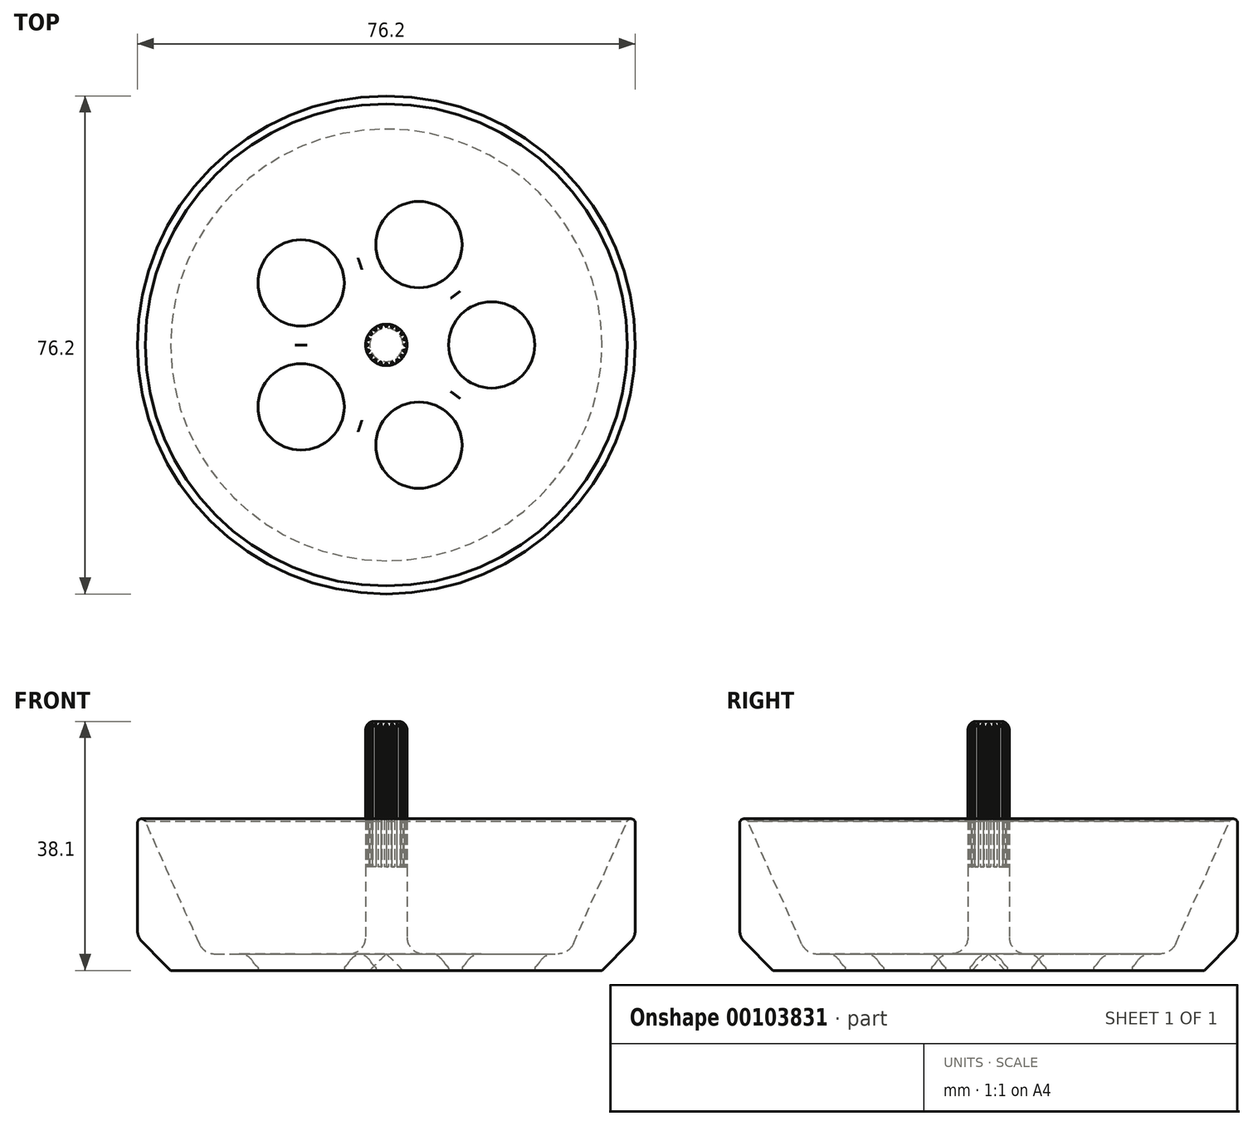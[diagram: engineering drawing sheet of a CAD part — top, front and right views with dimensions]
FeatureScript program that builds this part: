
annotation { "Feature Type Name" : "Feature", "Feature Type Description" : "" }
export const myFeature = defineFeature(function(context is Context, id is Id, definition is map)
    precondition{}
    {
        {
            var Q0;
            Q0=qCreatedBy(makeId("Front.planeOp"),FACE);
            var sketch = newSketch(context, id + "F0", { "sketchPlane" : qUnion([Q0])});
            skLineSegment(sketch, "E0", {"start": v(0, 0) * mm, "end": v(0, 38.1) * mm});
            skLineSegment(sketch, "E1", {"start": v(0, 38.1) * mm, "end": v(1.9, 38.1) * mm});
            skLineSegment(sketch, "E2", {"start": v(38.1, 22.56) * mm, "end": v(38.1, 6.13) * mm});
            skLineSegment(sketch, "E3", {"start": v(2.54, 0) * mm, "end": v(0, 2.54) * mm});
            skPoint(sketch, "E4.visualSharp", {"position": v(3.18, 2.54) * mm});
            skPoint(sketch, "E5.visualSharp", {"position": v(27.94, 2.54) * mm});
            skPoint(sketch, "E6.visualSharp", {"position": v(38.1, 25.4) * mm});
            skArc(sketch, "E6.filletArc", {"start": v(38.1, 22.56) * mm, "mid": v(37.6, 23.18) * mm, "end": v(36.9, 22.83) * mm});
            skPoint(sketch, "E7", {"position": v(16.72, 2.54) * mm});
            skArc(sketch, "E8", {"start": v(8.8, 1.29) * mm, "mid": v(9.08, 0.9) * mm, "end": v(9.43, 0.56) * mm});
            skArc(sketch, "E9", {"start": v(22.83, 0.56) * mm, "mid": v(23.18, 0.9) * mm, "end": v(23.47, 1.29) * mm});
            skLineSegment(sketch, "E10", {"start": v(36.9, 22.83) * mm, "end": v(28.6, 4.05) * mm});
            skLineSegment(sketch, "E11", {"start": v(3.18, 5.08) * mm, "end": v(3.17, 36.83) * mm});
            skLineSegment(sketch, "E12", {"start": v(5.72, 2.54) * mm, "end": v(6.6, 2.54) * mm});
            skLineSegment(sketch, "E13", {"start": v(25.65, 2.54) * mm, "end": v(26.28, 2.54) * mm});
            skPoint(sketch, "E14.visualSharp", {"position": v(23.83, 2.54) * mm});
            skArc(sketch, "E14.filletArc", {"start": v(25.65, 2.54) * mm, "mid": v(24.4, 2.2) * mm, "end": v(23.47, 1.29) * mm});
            skPoint(sketch, "E15.visualSharp", {"position": v(8.43, 2.54) * mm});
            skArc(sketch, "E15.filletArc", {"start": v(8.8, 1.29) * mm, "mid": v(7.86, 2.2) * mm, "end": v(6.6, 2.54) * mm});
            skLineSegment(sketch, "E16", {"start": v(6.6, 2.54) * mm, "end": v(25.65, 2.54) * mm});
            skLineSegment(sketch, "E17", {"start": v(2.54, 0) * mm, "end": v(9.53, 0) * mm});
            skLineSegment(sketch, "E18", {"start": v(22.73, 0) * mm, "end": v(33.02, 0) * mm});
            skLineSegment(sketch, "E19", {"start": v(16.13, 0) * mm, "end": v(16.13, 10.96) * mm});
            skArc(sketch, "E20.filletArc", {"start": v(3.18, 5.08) * mm, "mid": v(3.92, 3.28) * mm, "end": v(5.72, 2.54) * mm});
            skArc(sketch, "E21.filletArc", {"start": v(26.28, 2.54) * mm, "mid": v(27.67, 2.95) * mm, "end": v(28.6, 4.05) * mm});
            skPoint(sketch, "E22.visualSharp", {"position": v(3.17, 38.1) * mm});
            skArc(sketch, "E22.filletArc", {"start": v(3.17, 36.83) * mm, "mid": v(2.8, 37.73) * mm, "end": v(1.9, 38.1) * mm});
            skLineSegment(sketch, "E23", {"start": v(22.73, 0) * mm, "end": v(22.73, 0.36) * mm});
            skLineSegment(sketch, "E24.MirrorCS", {"start": v(9.53, 0) * mm, "end": v(9.53, 0.36) * mm});
            skPoint(sketch, "E25.orphan", {"position": v(11.05, 0) * mm});
            skPoint(sketch, "E26.end.orphan", {"position": v(21.2, 0) * mm});
            skLineSegment(sketch, "E27", {"start": v(9.53, 0) * mm, "end": v(22.73, 0) * mm});
            skPoint(sketch, "E28.newPointB", {"position": v(9.53, 6.48) * mm});
            skArc(sketch, "E28.filletArc", {"start": v(9.52, 0.36) * mm, "mid": v(9.5, 0.47) * mm, "end": v(9.43, 0.56) * mm});
            skPoint(sketch, "E29.newPointB", {"position": v(22.73, 6.48) * mm});
            skArc(sketch, "E29.filletArc", {"start": v(22.83, 0.56) * mm, "mid": v(22.76, 0.47) * mm, "end": v(22.73, 0.36) * mm});
            skLineSegment(sketch, "E30", {"start": v(33.02, 0) * mm, "end": v(37.36, 4.34) * mm});
            skPoint(sketch, "E31.orphan", {"position": v(38.1, 0) * mm});
            skPoint(sketch, "E32.visualSharp", {"position": v(38.1, 5.08) * mm});
            skArc(sketch, "E32.filletArc", {"start": v(37.36, 4.34) * mm, "mid": v(37.9, 5.16) * mm, "end": v(38.1, 6.13) * mm});
            skSolve(sketch);
        }
        {
            var Q0;
            {var subQ1=sQuery(id+"F0.wireOp",EDGE,"E1");Q0=makeQuery(id+"F0.imprint","IMPRINT",FACE,{"disambiguationData":[TD([[makeQuery(id+"F0.imprint","IMPRINT",EDGE,{"derivedFrom":subQ1}),-1.0]])]});}
            var Q1;
            {var subQ1=sQuery(id+"F0.wireOp",EDGE,"E8");Q1=makeQuery(id+"F0.imprint","IMPRINT",FACE,{"disambiguationData":[TD([[makeQuery(id+"F0.imprint","IMPRINT",EDGE,{"derivedFrom":subQ1}),1.0]])]});}
            var Q2;
            {var subQ1=sQuery(id+"F0.wireOp",EDGE,"E9");Q2=makeQuery(id+"F0.imprint","IMPRINT",FACE,{"disambiguationData":[TD([[makeQuery(id+"F0.imprint","IMPRINT",EDGE,{"derivedFrom":subQ1}),1.0]])]});}
            var Q3;
            Q3=makeQuery(id+"F0.imprint","IMPRINT",FACE,{"disambiguationData":[TD([[makeQuery(id+"F0.imprint","IMPRINT",EDGE,{"derivedFrom":sQuery(id+"F0.wireOp",EDGE,"E2")}),-1.0]])]});
            var Q4;
            Q4=sQuery(id+"F0.wireOp",EDGE,"E0");
            revolve(context, id + "F1", {"entities" : qUnion([Q0, Q1, Q2, Q3]), "axis" : qUnion([Q4]), "revolveType" : RevolveType.FULL});
        }
        {
            var Q0;
            {var subQ1=sQuery(id+"F0.wireOp",EDGE,"E8");Q0=makeQuery(id+"F0.imprint","IMPRINT",FACE,{"disambiguationData":[TD([[makeQuery(id+"F0.imprint","IMPRINT",EDGE,{"derivedFrom":subQ1}),1.0]])]});}
            var Q1;
            Q1=sQuery(id+"F0.wireOp",EDGE,"E19");
            revolve(context, id + "F2", {"entities" : qUnion([Q0]), "axis" : qUnion([Q1]), "revolveType" : RevolveType.FULL});
        }
        {
            var Q0;
            Q0=makeQuery(id+"F2.opRevolve","SWEPT_BODY",BODY,{"disambiguationData":[OSD([sQuery(id+"F0.wireOp",EDGE,"E8"),sQuery(id+"F0.wireOp",EDGE,"E15.filletArc"),sQuery(id+"F0.wireOp",EDGE,"E16"),sQuery(id+"F0.wireOp",EDGE,"E26"),sQuery(id+"F0.wireOp",EDGE,"E19")])]});
            var Q1;
            Q1=sQuery(id+"F0.wireOp",EDGE,"E0");
            circularPattern(context, id + "F3", {"entities" : qUnion([Q0]), "axis" : qUnion([Q1]), "angle" : 360 * degree, "instanceCount" : 5, "equalSpace" : true});
        }
        {
            var Q0;
            Q0=makeQuery(id+"F2.opRevolve","SWEPT_BODY",BODY,{"disambiguationData":[OSD([sQuery(id+"F0.wireOp",EDGE,"E8"),sQuery(id+"F0.wireOp",EDGE,"E15.filletArc"),sQuery(id+"F0.wireOp",EDGE,"E16"),sQuery(id+"F0.wireOp",EDGE,"E26"),sQuery(id+"F0.wireOp",EDGE,"E19")])]});
            var Q1;
            Q1=makeQuery(id+"F3.opPattern","COPY",BODY,{"derivedFrom":makeQuery(id+"F2.opRevolve","SWEPT_BODY",BODY,{"disambiguationData":[OSD([sQuery(id+"F0.wireOp",EDGE,"E8"),sQuery(id+"F0.wireOp",EDGE,"E15.filletArc"),sQuery(id+"F0.wireOp",EDGE,"E16"),sQuery(id+"F0.wireOp",EDGE,"E26"),sQuery(id+"F0.wireOp",EDGE,"E19")])]}),"instanceName":"1"});
            var Q2;
            Q2=makeQuery(id+"F3.opPattern","COPY",BODY,{"derivedFrom":makeQuery(id+"F2.opRevolve","SWEPT_BODY",BODY,{"disambiguationData":[OSD([sQuery(id+"F0.wireOp",EDGE,"E8"),sQuery(id+"F0.wireOp",EDGE,"E15.filletArc"),sQuery(id+"F0.wireOp",EDGE,"E16"),sQuery(id+"F0.wireOp",EDGE,"E26"),sQuery(id+"F0.wireOp",EDGE,"E19")])]}),"instanceName":"2"});
            var Q3;
            Q3=makeQuery(id+"F3.opPattern","COPY",BODY,{"derivedFrom":makeQuery(id+"F2.opRevolve","SWEPT_BODY",BODY,{"disambiguationData":[OSD([sQuery(id+"F0.wireOp",EDGE,"E8"),sQuery(id+"F0.wireOp",EDGE,"E15.filletArc"),sQuery(id+"F0.wireOp",EDGE,"E16"),sQuery(id+"F0.wireOp",EDGE,"E26"),sQuery(id+"F0.wireOp",EDGE,"E19")])]}),"instanceName":"3"});
            var Q4;
            Q4=makeQuery(id+"F3.opPattern","COPY",BODY,{"derivedFrom":makeQuery(id+"F2.opRevolve","SWEPT_BODY",BODY,{"disambiguationData":[OSD([sQuery(id+"F0.wireOp",EDGE,"E8"),sQuery(id+"F0.wireOp",EDGE,"E15.filletArc"),sQuery(id+"F0.wireOp",EDGE,"E16"),sQuery(id+"F0.wireOp",EDGE,"E26"),sQuery(id+"F0.wireOp",EDGE,"E19")])]}),"instanceName":"4"});
            var Q5;
            Q5=makeQuery(id+"F1.opRevolve","SWEPT_BODY",BODY,{"disambiguationData":[OSD([sQuery(id+"F0.wireOp",EDGE,"E0"),sQuery(id+"F0.wireOp",EDGE,"E1"),sQuery(id+"F0.wireOp",EDGE,"E2"),sQuery(id+"F0.wireOp",EDGE,"E3"),sQuery(id+"F0.wireOp",EDGE,"E6.filletArc"),sQuery(id+"F0.wireOp",EDGE,"E10"),sQuery(id+"F0.wireOp",EDGE,"E11"),sQuery(id+"F0.wireOp",EDGE,"E12"),sQuery(id+"F0.wireOp",EDGE,"E13"),sQuery(id+"F0.wireOp",EDGE,"E16"),sQuery(id+"F0.wireOp",EDGE,"E17"),sQuery(id+"F0.wireOp",EDGE,"E26"),sQuery(id+"F0.wireOp",EDGE,"E18"),sQuery(id+"F0.wireOp",EDGE,"E20.filletArc"),sQuery(id+"F0.wireOp",EDGE,"E21.filletArc")])]});
            booleanBodies(context, id + "F4", {"operationType" : BooleanOperationType.SUBTRACTION, "tools" : qUnion([Q0, Q1, Q2, Q3, Q4]), "targets" : qUnion([Q5])});
        }
        {
            var Q0;
            Q0=qCreatedBy(makeId("Top.planeOp"),FACE);
            var sketch = newSketch(context, id + "F5", { "sketchPlane" : qUnion([Q0])});
            skCircle(sketch, "E33", {"center": v(0, 0) * mm, "radius": 3.18 * mm});
            skLineSegment(sketch, "E34", {"start": v(0, 2.66) * mm, "end": v(0.3, 3.16) * mm});
            skLineSegment(sketch, "E35.MirrorCS", {"start": v(0, 2.66) * mm, "end": v(-0.3, 3.16) * mm});
            skLineSegment(sketch, "E36.1.0", {"start": v(-0.82, 2.53) * mm, "end": v(-0.68, 3.1) * mm});
            skLineSegment(sketch, "E36.1.1", {"start": v(-0.82, 2.53) * mm, "end": v(-1.27, 2.9) * mm});
            skLineSegment(sketch, "E36.2.0", {"start": v(-1.57, 2.16) * mm, "end": v(-1.6, 2.74) * mm});
            skLineSegment(sketch, "E36.2.1", {"start": v(-1.57, 2.16) * mm, "end": v(-2.1, 2.37) * mm});
            skLineSegment(sketch, "E36.3.0", {"start": v(-2.16, 1.57) * mm, "end": v(-2.37, 2.1) * mm});
            skLineSegment(sketch, "E36.3.1", {"start": v(-2.16, 1.57) * mm, "end": v(-2.74, 1.6) * mm});
            skLineSegment(sketch, "E36.4.0", {"start": v(-2.53, 0.82) * mm, "end": v(-2.9, 1.27) * mm});
            skLineSegment(sketch, "E36.4.1", {"start": v(-2.53, 0.82) * mm, "end": v(-3.1, 0.68) * mm});
            skLineSegment(sketch, "E36.5.0", {"start": v(-2.66, 0) * mm, "end": v(-3.16, 0.3) * mm});
            skLineSegment(sketch, "E36.5.1", {"start": v(-2.66, 0) * mm, "end": v(-3.16, -0.3) * mm});
            skLineSegment(sketch, "E36.6.0", {"start": v(-2.53, -0.82) * mm, "end": v(-3.1, -0.68) * mm});
            skLineSegment(sketch, "E36.6.1", {"start": v(-2.53, -0.82) * mm, "end": v(-2.9, -1.27) * mm});
            skLineSegment(sketch, "E36.7.0", {"start": v(-2.16, -1.57) * mm, "end": v(-2.74, -1.6) * mm});
            skLineSegment(sketch, "E36.7.1", {"start": v(-2.16, -1.57) * mm, "end": v(-2.37, -2.1) * mm});
            skLineSegment(sketch, "E36.8.0", {"start": v(-1.57, -2.16) * mm, "end": v(-2.1, -2.37) * mm});
            skLineSegment(sketch, "E36.8.1", {"start": v(-1.57, -2.16) * mm, "end": v(-1.6, -2.74) * mm});
            skLineSegment(sketch, "E36.9.0", {"start": v(-0.82, -2.53) * mm, "end": v(-1.27, -2.9) * mm});
            skLineSegment(sketch, "E36.9.1", {"start": v(-0.82, -2.53) * mm, "end": v(-0.68, -3.1) * mm});
            skLineSegment(sketch, "E36.10.0", {"start": v(0, -2.66) * mm, "end": v(-0.3, -3.16) * mm});
            skLineSegment(sketch, "E36.10.1", {"start": v(0, -2.66) * mm, "end": v(0.3, -3.16) * mm});
            skLineSegment(sketch, "E36.11.0", {"start": v(0.82, -2.53) * mm, "end": v(0.68, -3.1) * mm});
            skLineSegment(sketch, "E36.11.1", {"start": v(0.82, -2.53) * mm, "end": v(1.27, -2.9) * mm});
            skLineSegment(sketch, "E36.12.0", {"start": v(1.57, -2.16) * mm, "end": v(1.6, -2.74) * mm});
            skLineSegment(sketch, "E36.12.1", {"start": v(1.57, -2.16) * mm, "end": v(2.1, -2.37) * mm});
            skLineSegment(sketch, "E36.13.0", {"start": v(2.16, -1.57) * mm, "end": v(2.37, -2.1) * mm});
            skLineSegment(sketch, "E36.13.1", {"start": v(2.16, -1.57) * mm, "end": v(2.74, -1.6) * mm});
            skLineSegment(sketch, "E36.14.0", {"start": v(2.53, -0.82) * mm, "end": v(2.9, -1.27) * mm});
            skLineSegment(sketch, "E36.14.1", {"start": v(2.53, -0.82) * mm, "end": v(3.1, -0.68) * mm});
            skLineSegment(sketch, "E36.15.0", {"start": v(2.66, 0) * mm, "end": v(3.16, -0.3) * mm});
            skLineSegment(sketch, "E36.15.1", {"start": v(2.66, 0) * mm, "end": v(3.16, 0.3) * mm});
            skLineSegment(sketch, "E36.16.0", {"start": v(2.53, 0.82) * mm, "end": v(3.1, 0.68) * mm});
            skLineSegment(sketch, "E36.16.1", {"start": v(2.53, 0.82) * mm, "end": v(2.9, 1.27) * mm});
            skLineSegment(sketch, "E36.17.0", {"start": v(2.16, 1.57) * mm, "end": v(2.74, 1.6) * mm});
            skLineSegment(sketch, "E36.17.1", {"start": v(2.16, 1.57) * mm, "end": v(2.37, 2.1) * mm});
            skLineSegment(sketch, "E36.18.0", {"start": v(1.57, 2.16) * mm, "end": v(2.1, 2.37) * mm});
            skLineSegment(sketch, "E36.18.1", {"start": v(1.57, 2.16) * mm, "end": v(1.6, 2.74) * mm});
            skLineSegment(sketch, "E36.19.0", {"start": v(0.82, 2.53) * mm, "end": v(1.27, 2.9) * mm});
            skLineSegment(sketch, "E36.19.1", {"start": v(0.82, 2.53) * mm, "end": v(0.68, 3.1) * mm});
            skSolve(sketch);
        }
        {
            var Q0;
            {var subQ0=sQuery(id+"F5.wireOp",EDGE,"E36.3.0");Q0=makeQuery(id+"F5.imprint","IMPRINT",FACE,{"disambiguationData":[TD([[makeQuery(id+"F5.imprint","IMPRINT",EDGE,{"derivedFrom":subQ0}),1.0]])]});}
            var Q1;
            {var subQ0=sQuery(id+"F5.wireOp",EDGE,"E36.4.0");Q1=makeQuery(id+"F5.imprint","IMPRINT",FACE,{"disambiguationData":[TD([[makeQuery(id+"F5.imprint","IMPRINT",EDGE,{"derivedFrom":subQ0}),1.0]])]});}
            var Q2;
            {var subQ0=sQuery(id+"F5.wireOp",EDGE,"E36.5.0");Q2=makeQuery(id+"F5.imprint","IMPRINT",FACE,{"disambiguationData":[TD([[makeQuery(id+"F5.imprint","IMPRINT",EDGE,{"derivedFrom":subQ0}),1.0]])]});}
            var Q3;
            {var subQ0=sQuery(id+"F5.wireOp",EDGE,"E36.6.0");Q3=makeQuery(id+"F5.imprint","IMPRINT",FACE,{"disambiguationData":[TD([[makeQuery(id+"F5.imprint","IMPRINT",EDGE,{"derivedFrom":subQ0}),1.0]])]});}
            var Q4;
            {var subQ0=sQuery(id+"F5.wireOp",EDGE,"E36.7.0");Q4=makeQuery(id+"F5.imprint","IMPRINT",FACE,{"disambiguationData":[TD([[makeQuery(id+"F5.imprint","IMPRINT",EDGE,{"derivedFrom":subQ0}),1.0]])]});}
            var Q5;
            {var subQ0=sQuery(id+"F5.wireOp",EDGE,"E36.8.0");Q5=makeQuery(id+"F5.imprint","IMPRINT",FACE,{"disambiguationData":[TD([[makeQuery(id+"F5.imprint","IMPRINT",EDGE,{"derivedFrom":subQ0}),1.0]])]});}
            var Q6;
            {var subQ0=sQuery(id+"F5.wireOp",EDGE,"E36.9.0");Q6=makeQuery(id+"F5.imprint","IMPRINT",FACE,{"disambiguationData":[TD([[makeQuery(id+"F5.imprint","IMPRINT",EDGE,{"derivedFrom":subQ0}),1.0]])]});}
            var Q7;
            {var subQ0=sQuery(id+"F5.wireOp",EDGE,"E36.10.0");Q7=makeQuery(id+"F5.imprint","IMPRINT",FACE,{"disambiguationData":[TD([[makeQuery(id+"F5.imprint","IMPRINT",EDGE,{"derivedFrom":subQ0}),1.0]])]});}
            var Q8;
            {var subQ0=sQuery(id+"F5.wireOp",EDGE,"E36.11.0");Q8=makeQuery(id+"F5.imprint","IMPRINT",FACE,{"disambiguationData":[TD([[makeQuery(id+"F5.imprint","IMPRINT",EDGE,{"derivedFrom":subQ0}),1.0]])]});}
            var Q9;
            {var subQ0=sQuery(id+"F5.wireOp",EDGE,"E36.12.0");Q9=makeQuery(id+"F5.imprint","IMPRINT",FACE,{"disambiguationData":[TD([[makeQuery(id+"F5.imprint","IMPRINT",EDGE,{"derivedFrom":subQ0}),1.0]])]});}
            var Q10;
            {var subQ0=sQuery(id+"F5.wireOp",EDGE,"E36.13.0");Q10=makeQuery(id+"F5.imprint","IMPRINT",FACE,{"disambiguationData":[TD([[makeQuery(id+"F5.imprint","IMPRINT",EDGE,{"derivedFrom":subQ0}),1.0]])]});}
            var Q11;
            {var subQ0=sQuery(id+"F5.wireOp",EDGE,"E36.14.0");Q11=makeQuery(id+"F5.imprint","IMPRINT",FACE,{"disambiguationData":[TD([[makeQuery(id+"F5.imprint","IMPRINT",EDGE,{"derivedFrom":subQ0}),1.0]])]});}
            var Q12;
            {var subQ0=sQuery(id+"F5.wireOp",EDGE,"E36.15.0");Q12=makeQuery(id+"F5.imprint","IMPRINT",FACE,{"disambiguationData":[TD([[makeQuery(id+"F5.imprint","IMPRINT",EDGE,{"derivedFrom":subQ0}),1.0]])]});}
            var Q13;
            {var subQ0=sQuery(id+"F5.wireOp",EDGE,"E36.16.0");Q13=makeQuery(id+"F5.imprint","IMPRINT",FACE,{"disambiguationData":[TD([[makeQuery(id+"F5.imprint","IMPRINT",EDGE,{"derivedFrom":subQ0}),1.0]])]});}
            var Q14;
            {var subQ0=sQuery(id+"F5.wireOp",EDGE,"E36.17.0");Q14=makeQuery(id+"F5.imprint","IMPRINT",FACE,{"disambiguationData":[TD([[makeQuery(id+"F5.imprint","IMPRINT",EDGE,{"derivedFrom":subQ0}),1.0]])]});}
            var Q15;
            {var subQ0=sQuery(id+"F5.wireOp",EDGE,"E36.18.0");Q15=makeQuery(id+"F5.imprint","IMPRINT",FACE,{"disambiguationData":[TD([[makeQuery(id+"F5.imprint","IMPRINT",EDGE,{"derivedFrom":subQ0}),1.0]])]});}
            var Q16;
            {var subQ0=sQuery(id+"F5.wireOp",EDGE,"E36.19.0");Q16=makeQuery(id+"F5.imprint","IMPRINT",FACE,{"disambiguationData":[TD([[makeQuery(id+"F5.imprint","IMPRINT",EDGE,{"derivedFrom":subQ0}),1.0]])]});}
            var Q17;
            {var subQ0=sQuery(id+"F5.wireOp",EDGE,"E34");Q17=makeQuery(id+"F5.imprint","IMPRINT",FACE,{"disambiguationData":[TD([[makeQuery(id+"F5.imprint","IMPRINT",EDGE,{"derivedFrom":subQ0}),1.0]])]});}
            var Q18;
            {var subQ0=sQuery(id+"F5.wireOp",EDGE,"E36.1.0");Q18=makeQuery(id+"F5.imprint","IMPRINT",FACE,{"disambiguationData":[TD([[makeQuery(id+"F5.imprint","IMPRINT",EDGE,{"derivedFrom":subQ0}),1.0]])]});}
            var Q19;
            {var subQ0=sQuery(id+"F5.wireOp",EDGE,"E36.2.0");Q19=makeQuery(id+"F5.imprint","IMPRINT",FACE,{"disambiguationData":[TD([[makeQuery(id+"F5.imprint","IMPRINT",EDGE,{"derivedFrom":subQ0}),1.0]])]});}
            extrude(context, id + "F6", {"entities" : qUnion([Q0, Q1, Q2, Q3, Q4, Q5, Q6, Q7, Q8, Q9, Q10, Q11, Q12, Q13, Q14, Q15, Q16, Q17, Q18, Q19]), "depth" : 42.16 * mm, "hasSecondDirection" : true, "secondDirectionOppositeDirection" : false, "secondDirectionDepth" : 15.88 * mm});
        }
        {
            var Q0;
            Q0=makeQuery(id+"F6.opExtrude","SWEPT_BODY",BODY,{"disambiguationData":[OSD([sQuery(id+"F5.wireOp",EDGE,"E33"),sQuery(id+"F5.wireOp",EDGE,"E36.16.0"),sQuery(id+"F5.wireOp",EDGE,"E36.16.1")])]});
            var Q1;
            Q1=makeQuery(id+"F6.opExtrude","SWEPT_BODY",BODY,{"disambiguationData":[OSD([sQuery(id+"F5.wireOp",EDGE,"E33"),sQuery(id+"F5.wireOp",EDGE,"E36.17.0"),sQuery(id+"F5.wireOp",EDGE,"E36.17.1")])]});
            var Q2;
            Q2=makeQuery(id+"F6.opExtrude","SWEPT_BODY",BODY,{"disambiguationData":[OSD([sQuery(id+"F5.wireOp",EDGE,"E33"),sQuery(id+"F5.wireOp",EDGE,"E36.18.0"),sQuery(id+"F5.wireOp",EDGE,"E36.18.1")])]});
            var Q3;
            Q3=makeQuery(id+"F6.opExtrude","SWEPT_BODY",BODY,{"disambiguationData":[OSD([sQuery(id+"F5.wireOp",EDGE,"E33"),sQuery(id+"F5.wireOp",EDGE,"E36.19.0"),sQuery(id+"F5.wireOp",EDGE,"E36.19.1")])]});
            var Q4;
            Q4=makeQuery(id+"F6.opExtrude","SWEPT_BODY",BODY,{"disambiguationData":[OSD([sQuery(id+"F5.wireOp",EDGE,"E33"),sQuery(id+"F5.wireOp",EDGE,"E34"),sQuery(id+"F5.wireOp",EDGE,"E35.MirrorCS")])]});
            var Q5;
            Q5=makeQuery(id+"F6.opExtrude","SWEPT_BODY",BODY,{"disambiguationData":[OSD([sQuery(id+"F5.wireOp",EDGE,"E33"),sQuery(id+"F5.wireOp",EDGE,"E36.1.0"),sQuery(id+"F5.wireOp",EDGE,"E36.1.1")])]});
            var Q6;
            Q6=makeQuery(id+"F6.opExtrude","SWEPT_BODY",BODY,{"disambiguationData":[OSD([sQuery(id+"F5.wireOp",EDGE,"E33"),sQuery(id+"F5.wireOp",EDGE,"E36.2.0"),sQuery(id+"F5.wireOp",EDGE,"E36.2.1")])]});
            var Q7;
            Q7=makeQuery(id+"F6.opExtrude","SWEPT_BODY",BODY,{"disambiguationData":[OSD([sQuery(id+"F5.wireOp",EDGE,"E33"),sQuery(id+"F5.wireOp",EDGE,"E36.3.0"),sQuery(id+"F5.wireOp",EDGE,"E36.3.1")])]});
            var Q8;
            Q8=makeQuery(id+"F6.opExtrude","SWEPT_BODY",BODY,{"disambiguationData":[OSD([sQuery(id+"F5.wireOp",EDGE,"E33"),sQuery(id+"F5.wireOp",EDGE,"E36.4.0"),sQuery(id+"F5.wireOp",EDGE,"E36.4.1")])]});
            var Q9;
            Q9=makeQuery(id+"F6.opExtrude","SWEPT_BODY",BODY,{"disambiguationData":[OSD([sQuery(id+"F5.wireOp",EDGE,"E33"),sQuery(id+"F5.wireOp",EDGE,"E36.5.0"),sQuery(id+"F5.wireOp",EDGE,"E36.5.1")])]});
            var Q10;
            Q10=makeQuery(id+"F6.opExtrude","SWEPT_BODY",BODY,{"disambiguationData":[OSD([sQuery(id+"F5.wireOp",EDGE,"E33"),sQuery(id+"F5.wireOp",EDGE,"E36.6.0"),sQuery(id+"F5.wireOp",EDGE,"E36.6.1")])]});
            var Q11;
            Q11=makeQuery(id+"F6.opExtrude","SWEPT_BODY",BODY,{"disambiguationData":[OSD([sQuery(id+"F5.wireOp",EDGE,"E33"),sQuery(id+"F5.wireOp",EDGE,"E36.7.0"),sQuery(id+"F5.wireOp",EDGE,"E36.7.1")])]});
            var Q12;
            Q12=makeQuery(id+"F6.opExtrude","SWEPT_BODY",BODY,{"disambiguationData":[OSD([sQuery(id+"F5.wireOp",EDGE,"E33"),sQuery(id+"F5.wireOp",EDGE,"E36.8.0"),sQuery(id+"F5.wireOp",EDGE,"E36.8.1")])]});
            var Q13;
            Q13=makeQuery(id+"F6.opExtrude","SWEPT_BODY",BODY,{"disambiguationData":[OSD([sQuery(id+"F5.wireOp",EDGE,"E33"),sQuery(id+"F5.wireOp",EDGE,"E36.9.0"),sQuery(id+"F5.wireOp",EDGE,"E36.9.1")])]});
            var Q14;
            Q14=makeQuery(id+"F6.opExtrude","SWEPT_BODY",BODY,{"disambiguationData":[OSD([sQuery(id+"F5.wireOp",EDGE,"E33"),sQuery(id+"F5.wireOp",EDGE,"E36.10.0"),sQuery(id+"F5.wireOp",EDGE,"E36.10.1")])]});
            var Q15;
            Q15=makeQuery(id+"F6.opExtrude","SWEPT_BODY",BODY,{"disambiguationData":[OSD([sQuery(id+"F5.wireOp",EDGE,"E33"),sQuery(id+"F5.wireOp",EDGE,"E36.11.0"),sQuery(id+"F5.wireOp",EDGE,"E36.11.1")])]});
            var Q16;
            Q16=makeQuery(id+"F6.opExtrude","SWEPT_BODY",BODY,{"disambiguationData":[OSD([sQuery(id+"F5.wireOp",EDGE,"E33"),sQuery(id+"F5.wireOp",EDGE,"E36.12.0"),sQuery(id+"F5.wireOp",EDGE,"E36.12.1")])]});
            var Q17;
            Q17=makeQuery(id+"F6.opExtrude","SWEPT_BODY",BODY,{"disambiguationData":[OSD([sQuery(id+"F5.wireOp",EDGE,"E33"),sQuery(id+"F5.wireOp",EDGE,"E36.13.0"),sQuery(id+"F5.wireOp",EDGE,"E36.13.1")])]});
            var Q18;
            Q18=makeQuery(id+"F6.opExtrude","SWEPT_BODY",BODY,{"disambiguationData":[OSD([sQuery(id+"F5.wireOp",EDGE,"E33"),sQuery(id+"F5.wireOp",EDGE,"E36.14.0"),sQuery(id+"F5.wireOp",EDGE,"E36.14.1")])]});
            var Q19;
            Q19=makeQuery(id+"F6.opExtrude","SWEPT_BODY",BODY,{"disambiguationData":[OSD([sQuery(id+"F5.wireOp",EDGE,"E33"),sQuery(id+"F5.wireOp",EDGE,"E36.15.0"),sQuery(id+"F5.wireOp",EDGE,"E36.15.1")])]});
            var Q20;
            Q20=makeQuery(id+"F1.opRevolve","SWEPT_BODY",BODY,{"disambiguationData":[OSD([sQuery(id+"F0.wireOp",EDGE,"E0"),sQuery(id+"F0.wireOp",EDGE,"E1"),sQuery(id+"F0.wireOp",EDGE,"E2"),sQuery(id+"F0.wireOp",EDGE,"E3"),sQuery(id+"F0.wireOp",EDGE,"E6.filletArc"),sQuery(id+"F0.wireOp",EDGE,"E10"),sQuery(id+"F0.wireOp",EDGE,"E11"),sQuery(id+"F0.wireOp",EDGE,"E12"),sQuery(id+"F0.wireOp",EDGE,"E13"),sQuery(id+"F0.wireOp",EDGE,"E16"),sQuery(id+"F0.wireOp",EDGE,"E17"),sQuery(id+"F0.wireOp",EDGE,"E26"),sQuery(id+"F0.wireOp",EDGE,"E18"),sQuery(id+"F0.wireOp",EDGE,"E20.filletArc"),sQuery(id+"F0.wireOp",EDGE,"E21.filletArc"),sQuery(id+"F0.wireOp",EDGE,"E22.filletArc")])]});
            booleanBodies(context, id + "F7", {"operationType" : BooleanOperationType.SUBTRACTION, "tools" : qUnion([Q0, Q1, Q2, Q3, Q4, Q5, Q6, Q7, Q8, Q9, Q10, Q11, Q12, Q13, Q14, Q15, Q16, Q17, Q18, Q19]), "targets" : qUnion([Q20])});
        }
    });
